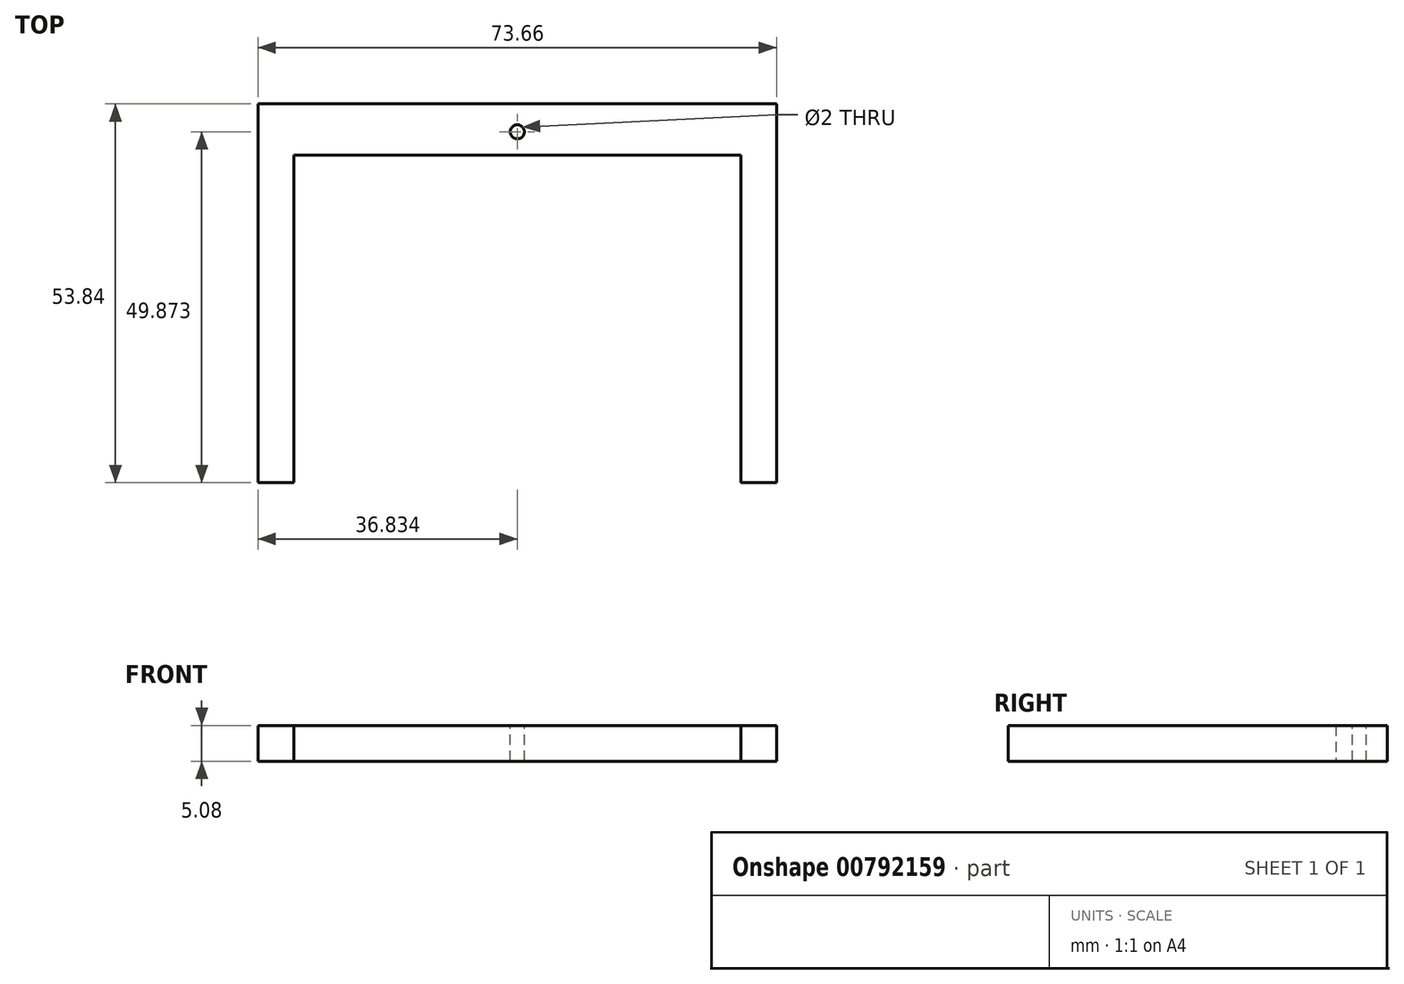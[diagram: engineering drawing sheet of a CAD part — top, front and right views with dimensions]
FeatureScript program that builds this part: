
annotation { "Feature Type Name" : "Feature", "Feature Type Description" : "" }
export const myFeature = defineFeature(function(context is Context, id is Id, definition is map)
    precondition{}
    {
        {
            var Q0;
            Q0=qCreatedBy(makeId("Top.planeOp"),FACE);
            var sketch = newSketch(context, id + "F0", { "sketchPlane" : qUnion([Q0])});
            skLineSegment(sketch, "E0", {"start": v(-18.75, -23.7) * mm, "end": v(-13.67, -23.7) * mm});
            skLineSegment(sketch, "E1", {"start": v(49.83, -23.7) * mm, "end": v(54.91, -23.7) * mm});
            skLineSegment(sketch, "E2", {"start": v(-18.75, -23.7) * mm, "end": v(-18.75, 30.14) * mm});
            skLineSegment(sketch, "E3", {"start": v(-18.75, 30.14) * mm, "end": v(54.91, 30.14) * mm});
            skLineSegment(sketch, "E4", {"start": v(54.91, 30.14) * mm, "end": v(54.91, -23.7) * mm});
            skLineSegment(sketch, "E5", {"start": v(49.83, -23.7) * mm, "end": v(49.83, 22.84) * mm});
            skLineSegment(sketch, "E6", {"start": v(49.83, 22.84) * mm, "end": v(-13.67, 22.84) * mm});
            skLineSegment(sketch, "E7", {"start": v(-13.67, 22.84) * mm, "end": v(-13.67, -23.7) * mm});
            skSolve(sketch);
        }
        {
            var Q0;
            Q0=qSketchRegion(id+"F0",true);
            extrude(context, id + "F1", {"entities" : qUnion([Q0]), "depth" : 5.08 * mm, "offsetDistance" : 25.4 * mm});
        }
        {
            var Q0;
            Q0=makeQuery(id+"F1.opExtrude","CAP_FACE",FACE,{"disambiguationData":[OSD([sQuery(id+"F0.wireOp",EDGE,"E0"),sQuery(id+"F0.wireOp",EDGE,"E1"),sQuery(id+"F0.wireOp",EDGE,"E2"),sQuery(id+"F0.wireOp",EDGE,"E3"),sQuery(id+"F0.wireOp",EDGE,"E4"),sQuery(id+"F0.wireOp",EDGE,"E5"),sQuery(id+"F0.wireOp",EDGE,"E6"),sQuery(id+"F0.wireOp",EDGE,"E7")])],"isStart":false});
            var sketch = newSketch(context, id + "F2", { "sketchPlane" : qUnion([Q0])});
            skCircle(sketch, "E8", {"center": v(18.08, 26.17) * mm, "radius": 1 * mm});
            skPoint(sketch, "E8.centerSnap0", {"position": v(18.08, 30.14) * mm});
            skSolve(sketch);
        }
        {
            var Q0;
            Q0 = qSketchRegion(id + "F2", true);
            extrude(context, id + "F3", {"entities" : qUnion([Q0]), "operationType" : NewBodyOperationType.REMOVE, "oppositeDirection" : true, "depth" : 25.4 * mm, "offsetDistance" : 25.4 * mm});
        }
    });
